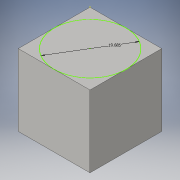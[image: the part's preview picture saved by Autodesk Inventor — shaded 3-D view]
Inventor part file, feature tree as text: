
AUTODESK INVENTOR PART (.ipt)
format: ipt  version: 2016 (Build 200138000, 138)  size: 84,480 bytes
history: native  units: in
note: dims shown in document units (in); Inventor stores cm internally (conversion verified against a paired STEP export)
features: sketch x2, extrude x1
ambient origin geometry x8: Origin, YZ Plane, XZ Plane, XY Plane, X Axis, Y Axis, Z Axis, Center Point
bodies: Body1 (feature_tree)
feature tree (3):
  extrude  "Extrusion4"  Depth=19.685in
  sketch  "Sketch5"  dims[d13=19.685in d14=0.0in d15=19.685in]
  sketch  "Sketch4"  dims[d11=19.685in d12=19.685in]
